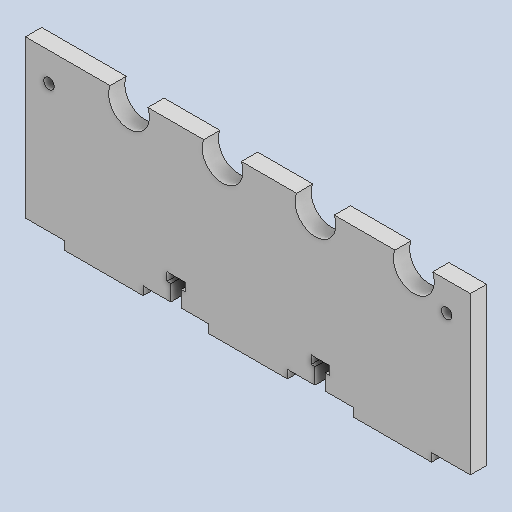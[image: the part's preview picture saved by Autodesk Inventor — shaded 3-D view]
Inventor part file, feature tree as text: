
AUTODESK INVENTOR PART (.ipt)
format: ipt  version: 2022 (Build 260153000, 153)  size: 200,192 bytes
history: native  units: mm
features: reference x16, other x7, extrude x2, sketch x2
ambient origin geometry x8: Origin, YZ Plane, XZ Plane, XY Plane, X Axis, Y Axis, Z Axis, Center Point
bodies: Body1 (feature_tree)
feature tree (27):
  extrude  "Extrusion3"  Depth=170.0mm
  extrude  "Extrusion4"  Depth=7.0mm
  sketch  "Sketch1"  dims[d2=170.0mm d4=0.3mm]
  reference  "Reference1"
  reference  "Reference2"
  reference  "Reference3"
  reference  "Reference4"
  reference  "Reference5"
  reference  "Reference6"
  reference  "Reference7"
  reference  "Reference8"
  reference  "Reference9"
  reference  "Reference10"
  reference  "Reference11"
  reference  "Reference12"
  reference  "Reference13"
  reference  "Reference14"
  reference  "Reference15"
  reference  "Reference16"
  sketch  "Sketch2"  dims[d5=0.3mm d6=0.3mm d7=0.3mm d17=4.0mm d19=8.0mm d24=9.0mm d42=60.0mm d43=30.0mm d44=3.2mm d45=15.0mm d46=75.186774mm d47=94.813226mm d48=9.0mm d49=8.0mm d50=4.0mm d51=3.2mm d52=15.0mm d53=25.093387mm d54=0.1mm d55=6.1mm d56=0.0mm d57=0.0mm d64=2.0mm d65=3.5mm d66=3.2mm d67=4.0mm d68=6.1mm d69=7.0mm d70=7.0mm d71=0.0mm d72=0.5mm d73=0.872665mm]
  other  "Caja_Reductora.iam"
  other  "Rodamiento_Ejes:1"
  other  "Rodamiento_Ejes:2"
  other  "Engranajes_1_5:1"
  other  "Engranajes_1_4:1"
  other  "Rodamiento_Ejes:8"
  other  "Rodamiento_Ejes:7"
